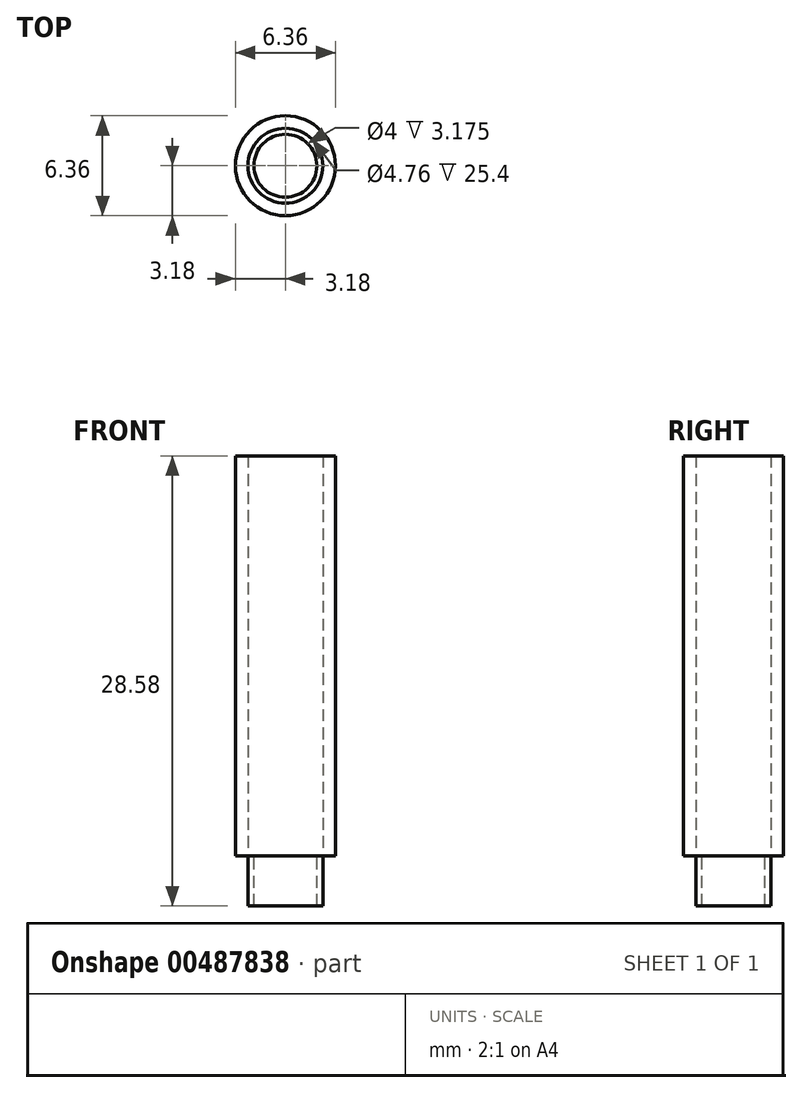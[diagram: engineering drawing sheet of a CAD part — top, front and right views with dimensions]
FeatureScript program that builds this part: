
annotation { "Feature Type Name" : "Feature", "Feature Type Description" : "" }
export const myFeature = defineFeature(function(context is Context, id is Id, definition is map)
    precondition{}
    {
        {
            var Q0;
            Q0=qCreatedBy(makeId("Top.planeOp"),FACE);
            var sketch = newSketch(context, id + "F0", { "sketchPlane" : qUnion([Q0])});
            skCircle(sketch, "E0", {"center": v(0, 0) * mm, "radius": 2.38 * mm});
            skCircle(sketch, "E1", {"center": v(0, 0) * mm, "radius": 3.18 * mm});
            skCircle(sketch, "E2", {"center": v(0, 0) * mm, "radius": 2 * mm});
            skSolve(sketch);
        }
        {
            var Q0;
            Q0=makeQuery(id+"F0.imprint","IMPRINT",FACE,{"disambiguationData":[TD([[makeQuery(id+"F0.imprint","IMPRINT",EDGE,{"derivedFrom":sQuery(id+"F0.wireOp",EDGE,"E0")}),-1.0]])]});
            extrude(context, id + "F1", {"entities" : qUnion([Q0]), "depth" : 25.4 * mm});
        }
        {
            var Q0;
            Q0=makeQuery(id+"F0.imprint","IMPRINT",FACE,{"disambiguationData":[TD([[makeQuery(id+"F0.imprint","IMPRINT",EDGE,{"derivedFrom":sQuery(id+"F0.wireOp",EDGE,"E0")}),1.0]])]});
            extrude(context, id + "F2", {"entities" : qUnion([Q0]), "oppositeDirection" : true, "depth" : 3.17 * mm});
        }
    });
